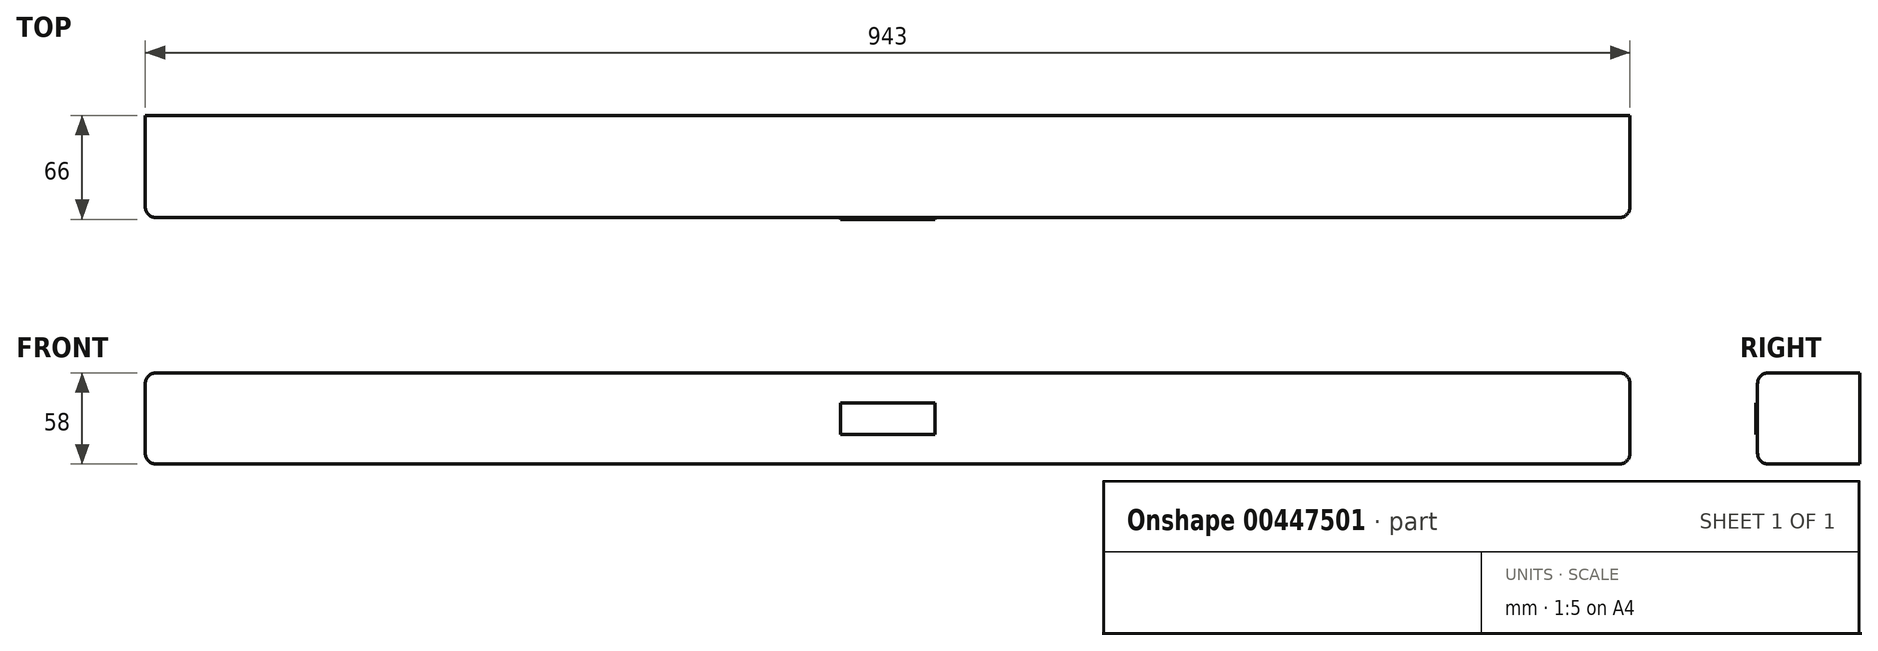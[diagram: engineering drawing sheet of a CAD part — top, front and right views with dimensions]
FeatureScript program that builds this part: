
annotation { "Feature Type Name" : "Feature", "Feature Type Description" : "" }
export const myFeature = defineFeature(function(context is Context, id is Id, definition is map)
    precondition{}
    {
        {
            var Q0;
            Q0=qCreatedBy(makeId("Front.planeOp"),FACE);
            var sketch = newSketch(context, id + "F0", { "sketchPlane" : qUnion([Q0])});
            skLineSegment(sketch, "E0.bottom", {"start": v(-471.5, 0) * mm, "end": v(471.5, 0) * mm});
            skLineSegment(sketch, "E0.top", {"start": v(-471.5, -58) * mm, "end": v(471.5, -58) * mm});
            skLineSegment(sketch, "E0.left", {"start": v(-471.5, 0) * mm, "end": v(-471.5, -58) * mm});
            skLineSegment(sketch, "E0.right", {"start": v(471.5, 0) * mm, "end": v(471.5, -58) * mm});
            skSolve(sketch);
        }
        {
            var Q0;
            Q0=makeQuery(id+"F0.imprint","IMPRINT",FACE,{"disambiguationData":[TD([[makeQuery(id+"F0.imprint","IMPRINT",EDGE,{"derivedFrom":sQuery(id+"F0.wireOp",EDGE,"E0.bottom")}),-1.0]])]});
            extrude(context, id + "F1", {"entities" : qUnion([Q0]), "depth" : 65 * mm});
        }
        {
            var Q0;
            Q0=makeQuery(id+"F1.opExtrude","CAP_EDGE",EDGE,{"disambiguationData":[OSD([sQuery(id+"F0.wireOp",EDGE,"E0.bottom")])],"isStart":false});
            var Q1;
            Q1=makeQuery(id+"F1.opExtrude","SWEPT_EDGE",EDGE,{"disambiguationData":[OSD([sQuery(id+"F0.wireOp",EDGE,"E0.bottom"),sQuery(id+"F0.wireOp",EDGE,"E0.right")])]});
            var Q2;
            Q2=makeQuery(id+"F1.opExtrude","CAP_EDGE",EDGE,{"disambiguationData":[OSD([sQuery(id+"F0.wireOp",EDGE,"E0.right")])],"isStart":false});
            var Q3;
            Q3=makeQuery(id+"F1.opExtrude","SWEPT_EDGE",EDGE,{"disambiguationData":[OSD([sQuery(id+"F0.wireOp",EDGE,"E0.top"),sQuery(id+"F0.wireOp",EDGE,"E0.right")])]});
            var Q4;
            Q4=makeQuery(id+"F1.opExtrude","CAP_EDGE",EDGE,{"disambiguationData":[OSD([sQuery(id+"F0.wireOp",EDGE,"E0.top")])],"isStart":false});
            var Q5;
            Q5=makeQuery(id+"F1.opExtrude","SWEPT_EDGE",EDGE,{"disambiguationData":[OSD([sQuery(id+"F0.wireOp",EDGE,"E0.bottom"),sQuery(id+"F0.wireOp",EDGE,"E0.left")])]});
            var Q6;
            Q6=makeQuery(id+"F1.opExtrude","SWEPT_EDGE",EDGE,{"disambiguationData":[OSD([sQuery(id+"F0.wireOp",EDGE,"E0.top"),sQuery(id+"F0.wireOp",EDGE,"E0.left")])]});
            var Q7;
            Q7=makeQuery(id+"F1.opExtrude","CAP_EDGE",EDGE,{"disambiguationData":[OSD([sQuery(id+"F0.wireOp",EDGE,"E0.left")])],"isStart":false});
            fillet(context, id + "F2", {"entities" : qUnion([Q0, Q1, Q2, Q3, Q4, Q5, Q6, Q7]), "radius" : 7 * mm, "tangentPropagation" : true, "allowEdgeOverflow" : false});
        }
        {
            var Q0;
            Q0=makeQuery(id+"F1.opExtrude","CAP_FACE",FACE,{"disambiguationData":[OSD([sQuery(id+"F0.wireOp",EDGE,"E0.bottom"),sQuery(id+"F0.wireOp",EDGE,"E0.top"),sQuery(id+"F0.wireOp",EDGE,"E0.left"),sQuery(id+"F0.wireOp",EDGE,"E0.right")])],"isStart":false});
            var sketch = newSketch(context, id + "F3", { "sketchPlane" : qUnion([Q0])});
            skLineSegment(sketch, "E1.bottom", {"start": v(-30, -19) * mm, "end": v(30, -19) * mm});
            skLineSegment(sketch, "E1.top", {"start": v(-30, -39) * mm, "end": v(30, -39) * mm});
            skLineSegment(sketch, "E1.left", {"start": v(-30, -19) * mm, "end": v(-30, -39) * mm});
            skLineSegment(sketch, "E1.right", {"start": v(30, -19) * mm, "end": v(30, -39) * mm});
            skLineSegment(sketch, "E2", {"start": v(0, 0) * mm, "end": v(0, -58) * mm, "construction": true});
            skPoint(sketch, "E2.endSnap0", {"position": v(0, -51) * mm});
            skPoint(sketch, "E3", {"position": v(0, -19) * mm});
            skLineSegment(sketch, "E4", {"start": v(-30, -39) * mm, "end": v(30, -19) * mm, "construction": true});
            skPoint(sketch, "E5", {"position": v(0, -29) * mm});
            skSolve(sketch);
        }
        {
            var Q0;
            Q0 = qSketchRegion(id + "F3", true);
            extrude(context, id + "F4", {"entities" : qUnion([Q0]), "operationType" : NewBodyOperationType.ADD, "depth" : 1 * mm});
        }
    });
